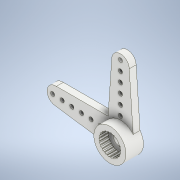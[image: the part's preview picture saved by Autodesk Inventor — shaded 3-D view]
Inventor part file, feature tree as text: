
AUTODESK INVENTOR PART (.ipt)
format: ipt  version: 2022 (Build 260153000, 153)  size: 229,888 bytes
history: mixed  units: in
note: dims shown in document units (in); Inventor stores cm internally (conversion verified against a paired STEP export)
features: sketch x2, pattern_circular x1, imported_body x1
ambient origin geometry x8: Origin, YZ Plane, XZ Plane, XY Plane, X Axis, Y Axis, Z Axis, Center Point
bodies: Solid1 (imported_parasolid), Body1 (imported_parasolid)
feature tree (4):
  sketch  "스케치1"
  sketch  "스케치2"
  pattern_circular  "원형 패턴1"  Count=2  [1 undecoded]
  imported_body  NMx_Import_Brep_tag  [imported B-rep: ~114 faces, bbox_mm=[17.544758, 18.291232, 3.8]]
note: 1 required parameter value undecoded (feature->parameter linkage not recoverable at this tier; creation-order binding heuristic only, values carry confidence <= 0.55)
